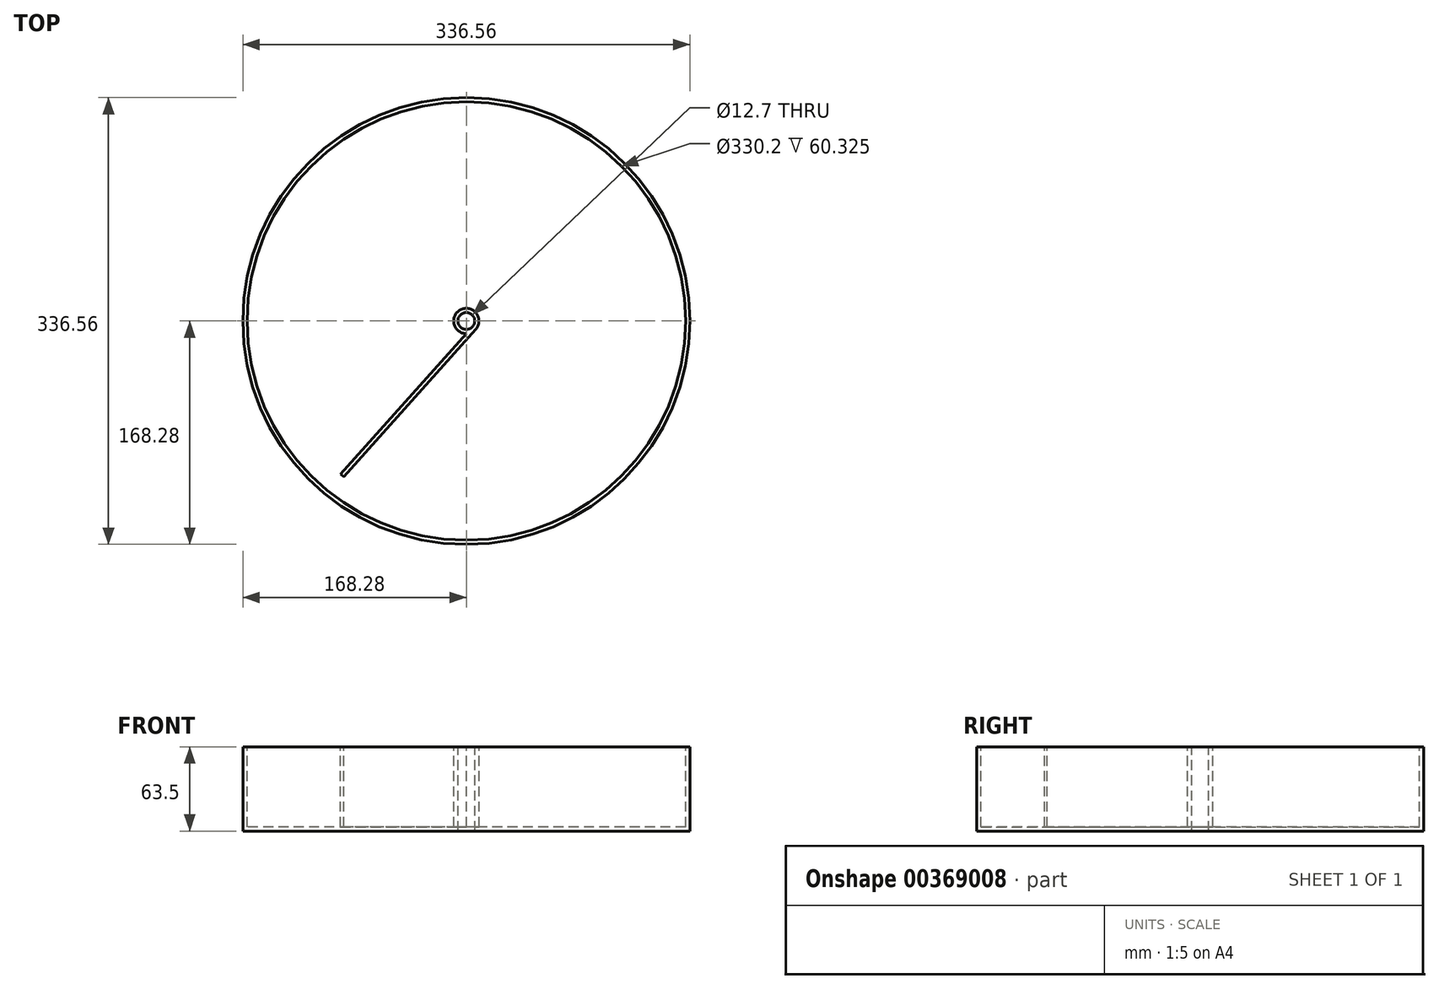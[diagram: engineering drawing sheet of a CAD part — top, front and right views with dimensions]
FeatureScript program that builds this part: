
annotation { "Feature Type Name" : "Feature", "Feature Type Description" : "" }
export const myFeature = defineFeature(function(context is Context, id is Id, definition is map)
    precondition{}
    {
        {
            var Q0;
            Q0=qCreatedBy(makeId("Front.planeOp"),FACE);
            var sketch = newSketch(context, id + "F0", { "sketchPlane" : qUnion([Q0])});
            skLineSegment(sketch, "E0.bottom", {"start": v(-6.35, 0) * mm, "end": v(-9.53, 0) * mm});
            skLineSegment(sketch, "E0.top", {"start": v(-6.35, 63.5) * mm, "end": v(-9.52, 63.5) * mm});
            skLineSegment(sketch, "E0.left", {"start": v(-6.35, 0) * mm, "end": v(-6.35, 63.5) * mm});
            skLineSegment(sketch, "E0.right", {"start": v(-9.52, 38.1) * mm, "end": v(-9.52, 63.5) * mm});
            skLineSegment(sketch, "E1.bottom", {"start": v(-9.53, 0) * mm, "end": v(-19.05, 0) * mm});
            skLineSegment(sketch, "E2.bottom", {"start": v(-19.05, 0) * mm, "end": v(-139.7, 0) * mm});
            skLineSegment(sketch, "E2.top", {"start": v(-18.93, 3.18) * mm, "end": v(-139.62, 3.18) * mm});
            skLineSegment(sketch, "E3.bottom", {"start": v(-139.7, 0) * mm, "end": v(-165.1, 0) * mm});
            skLineSegment(sketch, "E4.bottom", {"start": v(-165.1, 0) * mm, "end": v(-168.28, 0) * mm});
            skLineSegment(sketch, "E4.top", {"start": v(-165.1, 63.5) * mm, "end": v(-168.28, 63.5) * mm});
            skLineSegment(sketch, "E4.left", {"start": v(-165.1, 38.1) * mm, "end": v(-165.1, 63.5) * mm});
            skLineSegment(sketch, "E4.right", {"start": v(-168.28, 0) * mm, "end": v(-168.28, 63.5) * mm});
            skLineSegment(sketch, "E5", {"start": v(-9.52, 3.18) * mm, "end": v(-18.93, 3.18) * mm});
            skLineSegment(sketch, "E6", {"start": v(-9.53, 38.1) * mm, "end": v(-9.52, 3.18) * mm});
            skPoint(sketch, "E1.right.end.orphan", {"position": v(-19.05, 38.1) * mm});
            skLineSegment(sketch, "E7", {"start": v(-165.1, 38.1) * mm, "end": v(-165.1, 3.18) * mm});
            skLineSegment(sketch, "E8", {"start": v(-165.1, 3.18) * mm, "end": v(-139.62, 3.18) * mm});
            skSolve(sketch);
        }
        {
            var Q0;
            Q0=qCreatedBy(makeId("Front.planeOp"),FACE);
            var sketch = newSketch(context, id + "F1", { "sketchPlane" : qUnion([Q0])});
            skLineSegment(sketch, "E9", {"start": v(0, 46.12) * mm, "end": v(0, -40.85) * mm});
            skSolve(sketch);
        }
        {
            var Q0;
            Q0 = qSketchRegion(id + "F0", true);
            var Q1;
            Q1=sQuery(id+"F1.wireOp",EDGE,"E9");
            revolve(context, id + "F2", {"entities" : qUnion([Q0]), "axis" : qUnion([Q1]), "revolveType" : RevolveType.FULL});
        }
        {
            var Q0;
            Q0=makeQuery(id+"F2.opRevolve","SWEPT_FACE",FACE,{"disambiguationData":[OSD([sQuery(id+"F0.wireOp",EDGE,"E0.top")])]});
            var sketch = newSketch(context, id + "F3", { "sketchPlane" : qUnion([Q0])});
            skArc(sketch, "E10", {"start": v(7.1, -6.35) * mm, "mid": v(3.89, -8.7) * mm, "end": v(0, -9.52) * mm});
            skArc(sketch, "E11", {"start": v(-92.18, -117.35) * mm, "mid": v(-93.43, -116.36) * mm, "end": v(-94.66, -115.36) * mm});
            skLineSegment(sketch, "E12", {"start": v(0, -9.52) * mm, "end": v(-94.66, -115.36) * mm});
            skLineSegment(sketch, "E13", {"start": v(-92.18, -117.35) * mm, "end": v(7.1, -6.35) * mm});
            skSolve(sketch);
        }
        {
            var Q0;
            Q0 = qSketchRegion(id + "F3", true);
            extrude(context, id + "F4", {"entities" : qUnion([Q0]), "operationType" : NewBodyOperationType.ADD, "endBound" : BoundingType.UP_TO_NEXT, "oppositeDirection" : true, "depth" : 25.4 * mm});
        }
    });
